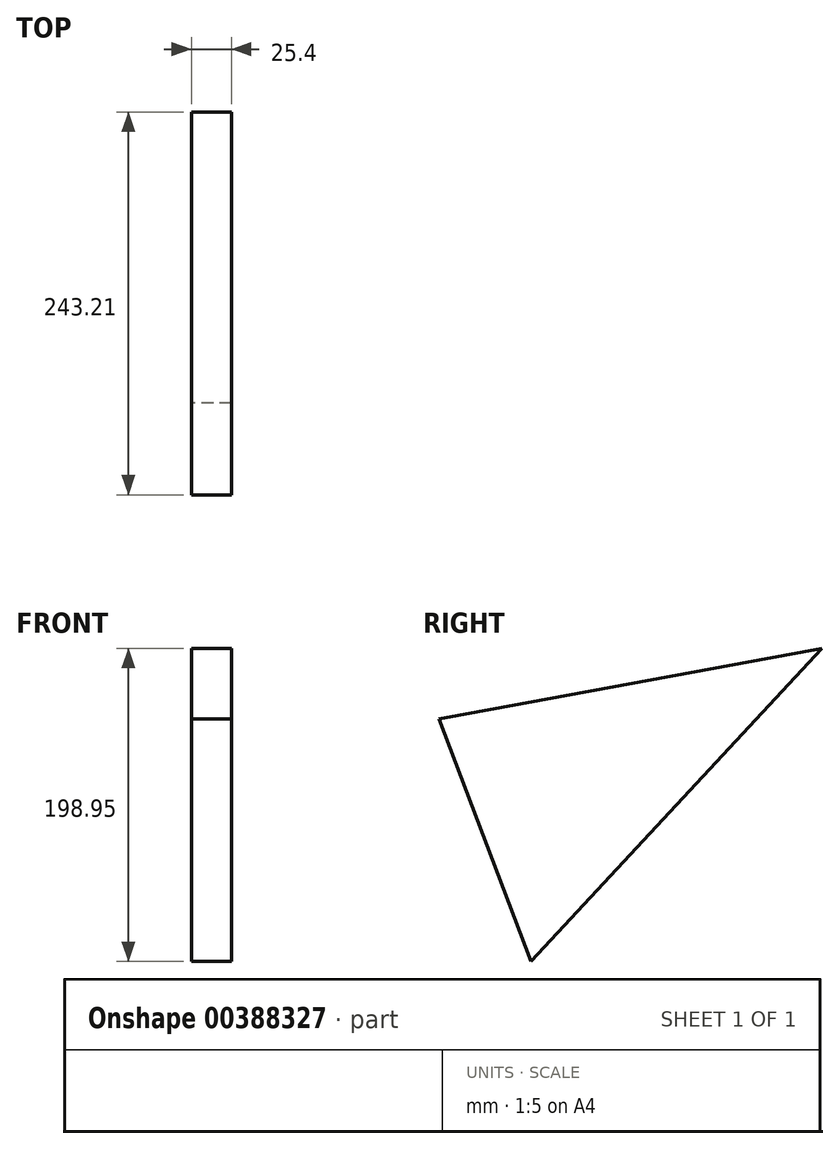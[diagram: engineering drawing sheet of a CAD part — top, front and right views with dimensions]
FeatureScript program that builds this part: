
annotation { "Feature Type Name" : "Feature", "Feature Type Description" : "" }
export const myFeature = defineFeature(function(context is Context, id is Id, definition is map)
    precondition{}
    {
        {
            var Q0;
            Q0=qCreatedBy(makeId("Right.planeOp"),FACE);
            var sketch = newSketch(context, id + "F0", { "sketchPlane" : qUnion([Q0])});
            skLineSegment(sketch, "E0", {"start": v(-68.72, 61.7) * mm, "end": v(12.74, -40.94) * mm});
            skLineSegment(sketch, "E1", {"start": v(12.74, -40.94) * mm, "end": v(-63.43, -27.66) * mm});
            skLineSegment(sketch, "E2", {"start": v(-63.43, -27.66) * mm, "end": v(-68.72, 61.7) * mm});
            skLineSegment(sketch, "E3", {"start": v(-45.74, 113.35) * mm, "end": v(-45.74, 133.7) * mm});
            skLineSegment(sketch, "E4", {"start": v(-45.74, 133.7) * mm, "end": v(197.47, 158) * mm});
            skLineSegment(sketch, "E5", {"start": v(197.47, 158) * mm, "end": v(-45.74, 113.35) * mm});
            skLineSegment(sketch, "E6", {"start": v(-45.74, 113.35) * mm, "end": v(-68.72, 61.7) * mm});
            skLineSegment(sketch, "E7", {"start": v(12.74, -40.94) * mm, "end": v(-45.74, 113.35) * mm});
            skLineSegment(sketch, "E8", {"start": v(12.74, -40.94) * mm, "end": v(197.47, 158) * mm});
            skSolve(sketch);
        }
        {
            var Q0;
            Q0=makeQuery(id+"F0.imprint","IMPRINT",FACE,{"disambiguationData":[TD([[makeQuery(id+"F0.imprint","IMPRINT",EDGE,{"derivedFrom":sQuery(id+"F0.wireOp",EDGE,"E5")}),1.0]])]});
            extrude(context, id + "F1", {"entities" : qUnion([Q0]), "depth" : 25.4 * mm});
        }
    });
